# Revit family: JCP (With Strainer)
name_source: partatom
category: Mechanical Equipment
units: mm (PartAtom-declared; Revit-internal decimal feet)

## family parameters
Always vertical = Yes
Classification = Pump
Cut with Voids When Loaded = No
OmniClass Number = 23.60.30.21
OmniClass Title = Pumps
Part Type = Normal
Room Calculation Point = Yes
Round Connector Dimension = Use Radius
Shared = No
Work Plane-Based = No

## types (6) — shared parameters
Anchor Hole Diameter = 3/8"
Assembly Code = D2090400
Discharge Height = 16 3/8"
Distance Between Anchor Points = 3 1/2"
Floor to Suction (Center) = 5 3/4"
Fluidra_Cos ϕ = 100.00%
Fluidra_Current = 0 A
Fluidra_Frequency = 60 Hz
Fluidra_Manufacturer = Fluidra
Fluidra_Number_of_Flange_Bolts = 8
Front to Discharge (Center) = 20"
Manufacturer = Fluidra
Pump Body = Fluidra Pump Body
Strainer Height = 21 19/32"
Strainer Tab Width = 17 1/4"
URL = https://www.jandy.com

## per-type parameters (varying)
| type | Anchor Point Width | Base Offset | Description | Ebox A | Ebox B | Fluidra_Description | Fluidra_Horsepower | Fluidra_Model | Fluidra_Phase | Fluidra_Voltage | Fluidra_Voltage (High) | Fluidra_Weight | Front to Anchor Point (Center) | Model | Motor | Motor Length | Pump Length | Pump Width (At Electrical Box) |
| JCP 5HP 208V 3PH | 9 3/4" | 32 1/4" | JCP Pump 5HP 3 Phase with Strainer | -12" | -8 1/2" | JCP Pump 5HP 3 Phase with Strainer | 5 hp | JCP053ATS | 3 | 208 V | 460 V | 169.00 lb | 33" | JCP053ATS | Fluidra 3 Ph Motor | 12" | 41 3/4" | 12 1/2" |
| JCP 7.5HP 208V 3PH | 10 3/4" | 33 1/4" | JCP Pump 7HP 3 Phase with Strainer | -13 3/4" | -10 1/4" | JCP Pump 7HP 3 Phase with Strainer | 8 hp | JCP073ATS | 3 | 208 V | 460 V | 201.00 lb | 34" | JCP073ATS | Fluidra 3 Ph Motor | 13 3/4" | 43 1/2" | 13 1/2" |
| JCP 10HP 208V 3PH | 10 3/4" | 33 1/4" | JCP Pump 10HP 3 Phase with Strainer | -13 3/4" | -10 1/4" | JCP Pump 10HP 3 Phase with Strainer | 10 hp | JCP103ATS | 3 | 208 V | 460 V | 209.00 lb | 34" | JCP103ATS | Fluidra 3 Ph Motor | 13 3/4" | 43 1/2" | 13 1/2" |
| JCP 15HP 208V 3PH | 10 3/4" | 33 1/4" | JCP Pump 15HP 3 Phase with Strainer | -16 1/4" | -12 3/4" | JCP Pump 15HP 3 Phase with Strainer | 15 hp | JCP153ATS | 3 | 208 V | 460 V | 249.00 lb | 34" | JCP153ATS | Fluidra 3 Ph Motor | 16 1/4" | 46" | 13 1/2" |
| JCP 5HP 230V 1PH | 9 3/4" | 32 1/4" | JCP Pump 5HP 1 Phase with Strainer | -13 1/2" | -10" | JCP Pump 5HP 1 Phase with Strainer | 5 hp | JCP051CTS | 1 | 230 V | 0 V | 178.00 lb | 33" | JCP051CTS | Fluidra 1 Ph Motor | 13 1/2" | 43 1/4" | 12 1/2" |
| JCP 7.5HP 230V 1PH | 10 3/4" | 33 1/4" | JCP Pump 7HP 1 Phase with Strainer | -12 1/4" | -8 3/4" | JCP Pump 7HP 1 Phase with Strainer | 8 hp | JCP071BDS | 1 | 230 V | 0 V | 197.00 lb | 34" | JCP071BDS | Fluidra 1 Ph Motor | 12 1/4" | 42" | 13 1/2" |

## geometry (parser evidence)
native form markers: Blend x2, Sweep x21
no freeform markers — native parametric forms only
